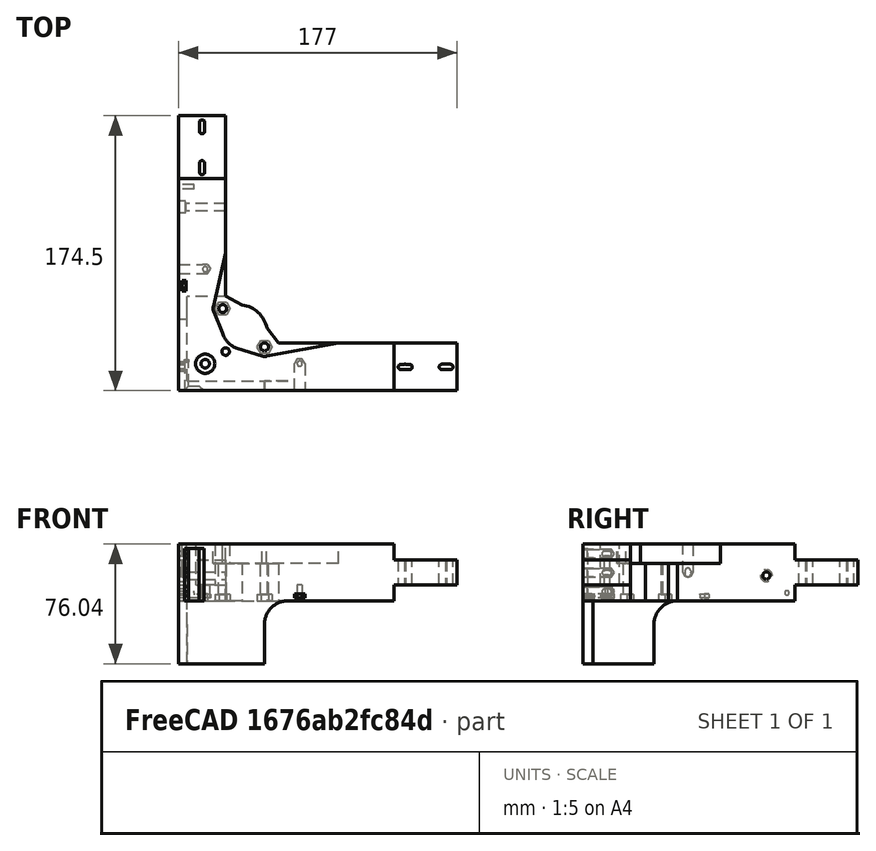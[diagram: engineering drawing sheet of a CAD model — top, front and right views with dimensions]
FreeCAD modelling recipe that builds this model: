
FCSTD DOCUMENT  (FreeCAD 2024.1R35694 (Git))
Label: bottom_front_left_frame
License: All rights reserved
LicenseURL: http://en.wikipedia.org/wiki/All_rights_reserved
objects: PartDesign::Pocket×2, Part::Feature×1, PartDesign::FeatureBase×1, PartDesign::Pad×1, PartDesign::Body×1
note: 9 computed .brp shape members not serialized (recipe doc carries the construction recipe); baked Part::Feature solids carry a one-line shape summary decoded from their .brp

FEATURE [Part::Feature] Body001
  shape: bbox 177 x 174.5 x 76.05 mm, 189 faces (baked)
FEATURE [PartDesign::FeatureBase] BaseFeature
  BaseFeature = -> Body001
FEATURE [PartDesign::Pocket] Pocket
  BaseFeature = -> BaseFeature
  Direction = (0,0,6414.47)
  Length = 0.3
  Length2 = 5
  Profile = -> BaseFeature [Face116]
  Refine = true
  Type = 0
FEATURE [PartDesign::Pad] Pad
  BaseFeature = -> Pocket
  Direction = (0,0,-10.8842)
  Length = 5.7
  Length2 = 10
  Profile = -> Pocket [Face195]
  Refine = true
  Type = 0
FEATURE [PartDesign::Pocket] Pocket001
  BaseFeature = -> Pad
  Direction = (0,0,6414.47)
  Length = 0.3
  Length2 = 5
  Profile = -> Pad [Face48]
  Refine = true
  Type = 0
FEATURE [PartDesign::Body] Body
  BaseFeature = -> Body001
  Group = -> [BaseFeature,Pocket,Pad,Pocket001]
  Origin = -> Origin
  Tip = -> Pocket001
